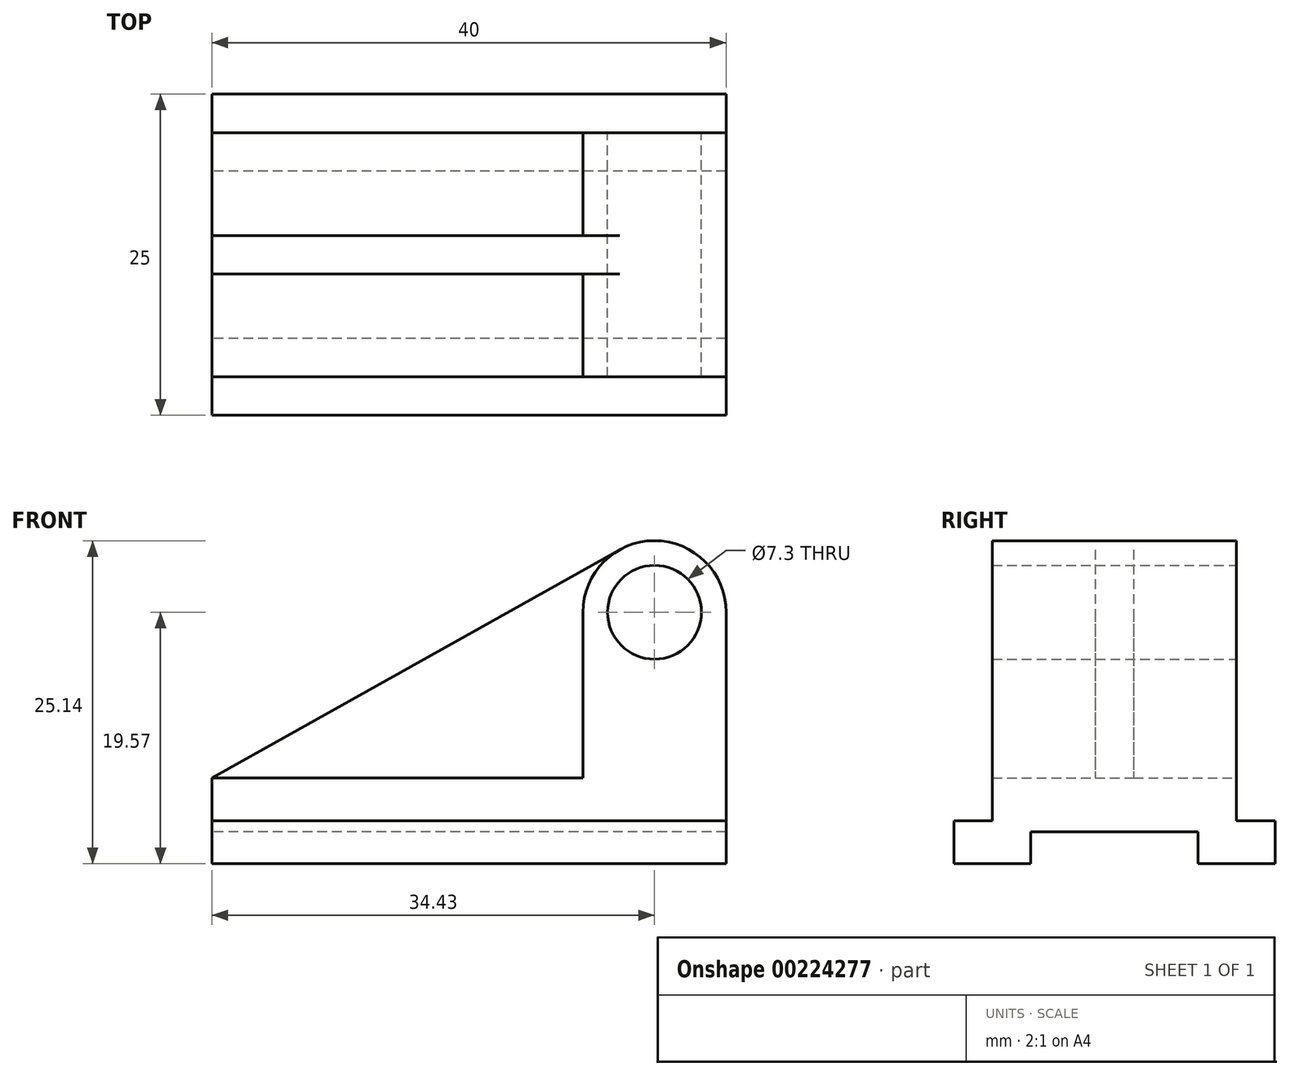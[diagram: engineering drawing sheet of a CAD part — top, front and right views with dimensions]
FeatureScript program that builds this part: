
annotation { "Feature Type Name" : "Feature", "Feature Type Description" : "" }
export const myFeature = defineFeature(function(context is Context, id is Id, definition is map)
    precondition{}
    {
        {
            var Q0;
            Q0=qCreatedBy(makeId("Front.planeOp"),FACE);
            var sketch = newSketch(context, id + "F0", { "sketchPlane" : qUnion([Q0])});
            skCircle(sketch, "E0", {"center": v(34.43, 19.57) * mm, "radius": 5.57 * mm});
            skCircle(sketch, "E1", {"center": v(34.43, 19.57) * mm, "radius": 3.65 * mm});
            skLineSegment(sketch, "E2", {"start": v(28.86, 19.57) * mm, "end": v(28.86, 6.68) * mm});
            skLineSegment(sketch, "E3", {"start": v(28.86, 6.68) * mm, "end": v(0, 6.68) * mm});
            skLineSegment(sketch, "E4", {"start": v(0, 6.68) * mm, "end": v(0, 0) * mm});
            skLineSegment(sketch, "E5", {"start": v(0, 0) * mm, "end": v(40, 0) * mm});
            skLineSegment(sketch, "E6", {"start": v(40, 0) * mm, "end": v(40, 19.57) * mm});
            skLineSegment(sketch, "E7", {"start": v(0, 3.34) * mm, "end": v(40, 3.34) * mm});
            skSolve(sketch);
        }
        {
            var Q0;
            Q0=makeQuery(id+"F0.imprint","IMPRINT",FACE,{"disambiguationData":[TD([[makeQuery(id+"F0.imprint","IMPRINT",EDGE,{"derivedFrom":sQuery(id+"F0.wireOp",EDGE,"E1")}),-1.0]])]});
            var Q1;
            {var subQ3=sQuery(id+"F0.wireOp",EDGE,"E2");Q1=makeQuery(id+"F0.imprint","IMPRINT",FACE,{"disambiguationData":[TD([[makeQuery(id+"F0.imprint","IMPRINT",EDGE,{"derivedFrom":subQ3}),1.0]])]});}
            extrude(context, id + "F1", {"entities" : qUnion([Q0, Q1]), "endBound" : BoundingType.SYMMETRIC, "depth" : 19 * mm});
        }
        {
            var Q0;
            {var subQ0=sQuery(id+"F0.wireOp",EDGE,"E5");Q0=makeQuery(id+"F0.imprint","IMPRINT",FACE,{"disambiguationData":[TD([[makeQuery(id+"F0.imprint","IMPRINT",EDGE,{"derivedFrom":subQ0}),1.0]])]});}
            extrude(context, id + "F2", {"entities" : qUnion([Q0]), "operationType" : NewBodyOperationType.ADD, "endBound" : BoundingType.SYMMETRIC, "depth" : 25 * mm});
        }
        {
            var Q0;
            Q0=qCreatedBy(makeId("Front.planeOp"),FACE);
            var sketch = newSketch(context, id + "F3", { "sketchPlane" : qUnion([Q0])});
            skLineSegment(sketch, "E8", {"start": v(31.7, 24.43) * mm, "end": v(0, 6.68) * mm});
            skCircle(sketch, "E9.0", {"center": v(34.43, 19.57) * mm, "radius": 5.57 * mm});
            skLineSegment(sketch, "E10.0", {"start": v(28.86, 19.57) * mm, "end": v(28.86, 6.68) * mm});
            skLineSegment(sketch, "E11.0", {"start": v(28.86, 6.68) * mm, "end": v(0, 6.68) * mm});
            skSolve(sketch);
        }
        {
            var Q0;
            {var subQ0=sQuery(id+"F3.wireOp",EDGE,"E8");Q0=makeQuery(id+"F3.imprint","IMPRINT",FACE,{"disambiguationData":[TD([[makeQuery(id+"F3.imprint","IMPRINT",EDGE,{"derivedFrom":subQ0}),1.0]])]});}
            extrude(context, id + "F4", {"entities" : qUnion([Q0]), "operationType" : NewBodyOperationType.ADD, "endBound" : BoundingType.SYMMETRIC, "depth" : 3 * mm});
        }
        {
            var Q0;
            {var subQ0=sQuery(id+"F0.wireOp",EDGE,"E4");Q0=makeQuery(id+"F2.boolean.opBoolean","MERGE",FACE,{"derivedFrom":[makeQuery(id+"F1.opExtrude","SWEPT_FACE",FACE,{"disambiguationData":[OSD([subQ0])]}),makeQuery(id+"F2.opExtrude","SWEPT_FACE",FACE,{"disambiguationData":[OSD([subQ0])]})]});}
            var sketch = newSketch(context, id + "F5", { "sketchPlane" : qUnion([Q0])});
            skLineSegment(sketch, "E12", {"start": v(-6.5, 0) * mm, "end": v(-6.5, 2.5) * mm});
            skLineSegment(sketch, "E13", {"start": v(-6.5, 2.5) * mm, "end": v(6.5, 2.5) * mm});
            skLineSegment(sketch, "E14", {"start": v(6.5, 2.5) * mm, "end": v(6.5, 0) * mm});
            skLineSegment(sketch, "E15", {"start": v(-6.5, 0) * mm, "end": v(6.5, 0) * mm});
            skSolve(sketch);
        }
        {
            var Q0;
            Q0=makeQuery(id+"F5.imprint","IMPRINT",FACE,{"disambiguationData":[TD([[makeQuery(id+"F5.imprint","IMPRINT",EDGE,{"derivedFrom":sQuery(id+"F5.wireOp",EDGE,"E12")}),-1.0]])]});
            extrude(context, id + "F6", {"entities" : qUnion([Q0]), "operationType" : NewBodyOperationType.REMOVE, "endBound" : BoundingType.THROUGH_ALL, "oppositeDirection" : true, "depth" : 25 * mm});
        }
    });
